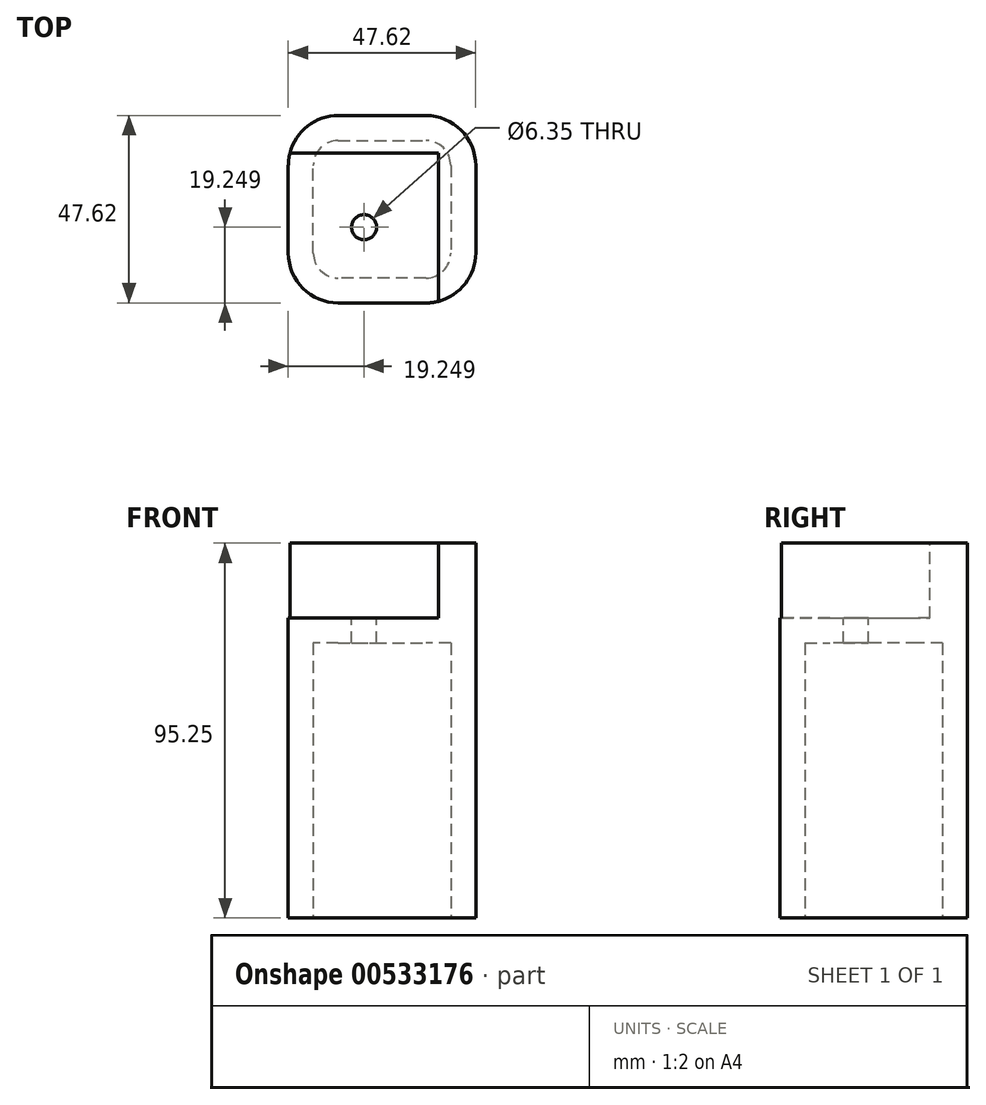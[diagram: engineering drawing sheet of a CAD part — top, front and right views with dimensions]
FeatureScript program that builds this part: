
annotation { "Feature Type Name" : "Feature", "Feature Type Description" : "" }
export const myFeature = defineFeature(function(context is Context, id is Id, definition is map)
    precondition{}
    {
        {
            var Q0;
            Q0=qCreatedBy(makeId("Top.planeOp"),FACE);
            var sketch = newSketch(context, id + "F0", { "sketchPlane" : qUnion([Q0])});
            skLineSegment(sketch, "E0.bottom", {"start": v(-11.11, 23.81) * mm, "end": v(11.11, 23.81) * mm});
            skLineSegment(sketch, "E0.top", {"start": v(-11.11, -23.81) * mm, "end": v(11.11, -23.81) * mm});
            skLineSegment(sketch, "E0.left", {"start": v(-23.81, 11.11) * mm, "end": v(-23.81, -11.11) * mm});
            skLineSegment(sketch, "E0.right", {"start": v(23.81, 11.11) * mm, "end": v(23.81, -11.11) * mm});
            skPoint(sketch, "E0.middle", {"position": v(0, 0) * mm});
            skLineSegment(sketch, "E1", {"start": v(-14.29, 23.4) * mm, "end": v(-14.29, -14.29) * mm});
            skLineSegment(sketch, "E2", {"start": v(-14.29, -14.29) * mm, "end": v(23.4, -14.29) * mm});
            skPoint(sketch, "E3.visualSharp", {"position": v(-23.81, 23.81) * mm});
            skArc(sketch, "E3.filletArc", {"start": v(-11.11, 23.81) * mm, "mid": v(-20.1, 20.1) * mm, "end": v(-23.81, 11.11) * mm});
            skPoint(sketch, "E4.visualSharp", {"position": v(23.81, 23.81) * mm});
            skArc(sketch, "E4.filletArc", {"start": v(23.81, 11.11) * mm, "mid": v(20.1, 20.1) * mm, "end": v(11.11, 23.81) * mm});
            skPoint(sketch, "E5.visualSharp", {"position": v(23.81, -23.81) * mm});
            skArc(sketch, "E5.filletArc", {"start": v(11.11, -23.81) * mm, "mid": v(20.1, -20.1) * mm, "end": v(23.81, -11.11) * mm});
            skPoint(sketch, "E6.visualSharp", {"position": v(-23.81, -23.81) * mm});
            skArc(sketch, "E6.filletArc", {"start": v(-23.81, -11.11) * mm, "mid": v(-20.1, -20.1) * mm, "end": v(-11.11, -23.81) * mm});
            skSolve(sketch);
        }
        {
            var Q0;
            {var subQ3=sQuery(id+"F0.wireOp",EDGE,"E0.top");Q0=makeQuery(id+"F0.imprint","IMPRINT",FACE,{"disambiguationData":[TD([[makeQuery(id+"F0.imprint","IMPRINT",EDGE,{"derivedFrom":subQ3}),1.0]])]});}
            var Q1;
            {var subQ3=sQuery(id+"F0.wireOp",EDGE,"E0.bottom");Q1=makeQuery(id+"F0.imprint","IMPRINT",FACE,{"disambiguationData":[TD([[makeQuery(id+"F0.imprint","IMPRINT",EDGE,{"derivedFrom":subQ3}),-1.0]])]});}
            extrude(context, id + "F1", {"entities" : qUnion([Q0, Q1]), "oppositeDirection" : true, "depth" : 95.25 * mm, "offsetDistance" : 25.4 * mm});
        }
        {
            var Q0;
            {var subQ3=sQuery(id+"F0.wireOp",EDGE,"E0.bottom");Q0=makeQuery(id+"F0.imprint","IMPRINT",FACE,{"disambiguationData":[TD([[makeQuery(id+"F0.imprint","IMPRINT",EDGE,{"derivedFrom":subQ3}),-1.0]])]});}
            extrude(context, id + "F2", {"entities" : qUnion([Q0]), "operationType" : NewBodyOperationType.REMOVE, "oppositeDirection" : true, "depth" : 19.05 * mm, "offsetDistance" : 25.4 * mm});
        }
        {
            var Q0;
            Q0=makeQuery(id+"F1.opExtrude","CAP_FACE",FACE,{"disambiguationData":[OSD([sQuery(id+"F0.wireOp",EDGE,"E0.bottom"),sQuery(id+"F0.wireOp",EDGE,"E0.top"),sQuery(id+"F0.wireOp",EDGE,"E0.left"),sQuery(id+"F0.wireOp",EDGE,"E0.right"),sQuery(id+"F0.wireOp",EDGE,"E3.filletArc"),sQuery(id+"F0.wireOp",EDGE,"E4.filletArc"),sQuery(id+"F0.wireOp",EDGE,"E5.filletArc"),sQuery(id+"F0.wireOp",EDGE,"E6.filletArc")])],"isStart":false});
            var sketch = newSketch(context, id + "F3", { "sketchPlane" : qUnion([Q0])});
            skLineSegment(sketch, "E7.0", {"start": v(-11.11, 23.81) * mm, "end": v(11.11, 23.81) * mm});
            skArc(sketch, "E8.0", {"start": v(-23.81, 11.11) * mm, "mid": v(-20.1, 20.1) * mm, "end": v(-11.11, 23.81) * mm});
            skLineSegment(sketch, "E9.0.0", {"start": v(-11.11, -23.81) * mm, "end": v(11.11, -23.81) * mm});
            skArc(sketch, "E9.0.1", {"start": v(11.11, -23.81) * mm, "mid": v(20.1, -20.1) * mm, "end": v(23.81, -11.11) * mm});
            skLineSegment(sketch, "E9.0.2", {"start": v(23.81, -11.11) * mm, "end": v(23.81, 11.11) * mm});
            skArc(sketch, "E9.0.3", {"start": v(23.81, 11.11) * mm, "mid": v(20.1, 20.1) * mm, "end": v(11.11, 23.81) * mm});
            skLineSegment(sketch, "E9.0.4", {"start": v(11.11, 23.81) * mm, "end": v(-11.11, 23.81) * mm});
            skArc(sketch, "E9.0.5", {"start": v(-11.11, 23.81) * mm, "mid": v(-20.1, 20.1) * mm, "end": v(-23.81, 11.11) * mm});
            skLineSegment(sketch, "E9.0.6", {"start": v(-23.81, 11.11) * mm, "end": v(-23.81, -11.11) * mm});
            skArc(sketch, "E9.0.7", {"start": v(-23.81, -11.11) * mm, "mid": v(-20.1, -20.1) * mm, "end": v(-11.11, -23.81) * mm});
            skArc(sketch, "E10.0", {"start": v(17.46, 11.11) * mm, "mid": v(15.6, 15.6) * mm, "end": v(11.11, 17.46) * mm});
            skLineSegment(sketch, "E10.1", {"start": v(17.46, -11.11) * mm, "end": v(17.46, 11.11) * mm});
            skLineSegment(sketch, "E10.2", {"start": v(11.11, 17.46) * mm, "end": v(-11.11, 17.46) * mm});
            skArc(sketch, "E10.3", {"start": v(11.11, -17.46) * mm, "mid": v(15.6, -15.6) * mm, "end": v(17.46, -11.11) * mm});
            skArc(sketch, "E10.4", {"start": v(-11.11, 17.46) * mm, "mid": v(-15.6, 15.6) * mm, "end": v(-17.46, 11.11) * mm});
            skLineSegment(sketch, "E10.5", {"start": v(-17.46, 11.11) * mm, "end": v(-17.46, -11.11) * mm});
            skArc(sketch, "E10.6", {"start": v(-17.46, -11.11) * mm, "mid": v(-15.6, -15.6) * mm, "end": v(-11.11, -17.46) * mm});
            skLineSegment(sketch, "E10.7", {"start": v(-11.11, -17.46) * mm, "end": v(11.11, -17.46) * mm});
            skSolve(sketch);
        }
        {
            var Q0;
            Q0=makeQuery(id+"F2.boolean.opBoolean","COPY",FACE,{"derivedFrom":makeQuery(id+"F2.opExtrude","CAP_FACE",FACE,{"disambiguationData":[OSD([sQuery(id+"F0.wireOp",EDGE,"E0.bottom"),sQuery(id+"F0.wireOp",EDGE,"E0.right"),sQuery(id+"F0.wireOp",EDGE,"E1"),sQuery(id+"F0.wireOp",EDGE,"E2"),sQuery(id+"F0.wireOp",EDGE,"E3.filletArc"),sQuery(id+"F0.wireOp",EDGE,"E4.filletArc"),sQuery(id+"F0.wireOp",EDGE,"E5.filletArc")])],"isStart":false})});
            cPlane(context, id + "F4", {"entities" : qUnion([Q0]), "cplaneType" : CPlaneType.OFFSET, "offset" : 6.35 * mm, "oppositeDirection" : true, "width" : 152.4 * mm, "height" : 152.4 * mm});
        }
        {
            var Q0;
            Q0=makeQuery(id+"F3.imprint","IMPRINT",FACE,{"disambiguationData":[TD([[makeQuery(id+"F3.imprint","IMPRINT",EDGE,{"derivedFrom":sQuery(id+"F3.wireOp",EDGE,"E10.0")}),1.0]])]});
            var Q1;
            Q1=qCreatedBy(id+"F4.planeOp",FACE);
            extrude(context, id + "F5", {"entities" : qUnion([Q0]), "operationType" : NewBodyOperationType.REMOVE, "endBound" : BoundingType.UP_TO_SURFACE, "oppositeDirection" : true, "depth" : 25.4 * mm, "endBoundEntityFace" : qUnion([Q1]), "offsetDistance" : 25.4 * mm});
        }
        {
            var Q0;
            Q0=makeQuery(id+"F2.boolean.opBoolean","COPY",FACE,{"derivedFrom":makeQuery(id+"F2.opExtrude","CAP_FACE",FACE,{"disambiguationData":[OSD([sQuery(id+"F0.wireOp",EDGE,"E0.bottom"),sQuery(id+"F0.wireOp",EDGE,"E0.right"),sQuery(id+"F0.wireOp",EDGE,"E1"),sQuery(id+"F0.wireOp",EDGE,"E2"),sQuery(id+"F0.wireOp",EDGE,"E3.filletArc"),sQuery(id+"F0.wireOp",EDGE,"E4.filletArc"),sQuery(id+"F0.wireOp",EDGE,"E5.filletArc")])],"isStart":false})});
            var sketch = newSketch(context, id + "F6", { "sketchPlane" : qUnion([Q0])});
            skPoint(sketch, "E11.centerSnap0", {"position": v(4.56, -14.29) * mm});
            skPoint(sketch, "E11.centerSnap1", {"position": v(-14.29, 4.56) * mm});
            skPoint(sketch, "E12", {"position": v(4.56, 4.56) * mm});
            skSolve(sketch);
        }
        {
            var Q0;
            Q0=sQuery(id+"F6.wireOp",VERTEX,"E12");
            var Q1;
            Q1=makeQuery(id+"F1.opExtrude","SWEPT_BODY",BODY,{"disambiguationData":[OSD([sQuery(id+"F0.wireOp",EDGE,"E0.bottom"),sQuery(id+"F0.wireOp",EDGE,"E0.top"),sQuery(id+"F0.wireOp",EDGE,"E0.left"),sQuery(id+"F0.wireOp",EDGE,"E0.right"),sQuery(id+"F0.wireOp",EDGE,"E3.filletArc"),sQuery(id+"F0.wireOp",EDGE,"E4.filletArc"),sQuery(id+"F0.wireOp",EDGE,"E5.filletArc"),sQuery(id+"F0.wireOp",EDGE,"E6.filletArc")])]});
            hole(context, id + "F7", {"style" : HoleStyle.C_BORE, "endStyle" : HoleEndStyle.BLIND, "holeDiameter" : 6.35 * mm, "cBoreDiameter" : 6.35 * mm, "cBoreDepth" : 6.35 * mm, "holeDepth" : 25.4 * mm, "isTappedThrough" : true, "tappedDepth" : 12.7 * mm, "tapClearance" : 3, "startFromSketch" : true, "locations" : qUnion([Q0]), "scope" : qUnion([Q1])});
        }
        {
            var Q0;
            Q0=qCreatedBy(makeId("Front.planeOp"),FACE);
            var sketch = newSketch(context, id + "F8", { "sketchPlane" : qUnion([Q0])});
            skLineSegment(sketch, "E13", {"start": v(0, 0) * mm, "end": v(0, -32.07) * mm, "construction": true});
            skLineSegment(sketch, "E14", {"start": v(0, 0) * mm, "end": v(0, 13.3) * mm, "construction": true});
            skSolve(sketch);
        }
        {
            var Q0;
            Q0=makeQuery(id+"F1.opExtrude","SWEPT_BODY",BODY,{"disambiguationData":[OSD([sQuery(id+"F0.wireOp",EDGE,"E0.bottom"),sQuery(id+"F0.wireOp",EDGE,"E0.top"),sQuery(id+"F0.wireOp",EDGE,"E0.left"),sQuery(id+"F0.wireOp",EDGE,"E0.right"),sQuery(id+"F0.wireOp",EDGE,"E3.filletArc"),sQuery(id+"F0.wireOp",EDGE,"E4.filletArc"),sQuery(id+"F0.wireOp",EDGE,"E5.filletArc"),sQuery(id+"F0.wireOp",EDGE,"E6.filletArc")])]});
            var Q1;
            Q1=sQuery(id+"F8.wireOp",EDGE,"E14");
            transform(context, id + "F9", {"entities" : qUnion([Q0]), "transformType" : TransformType.ROTATION, "transformAxis" : qUnion([Q1]), "angle" : 180 * degree, "makeCopy" : false});
        }
    });
